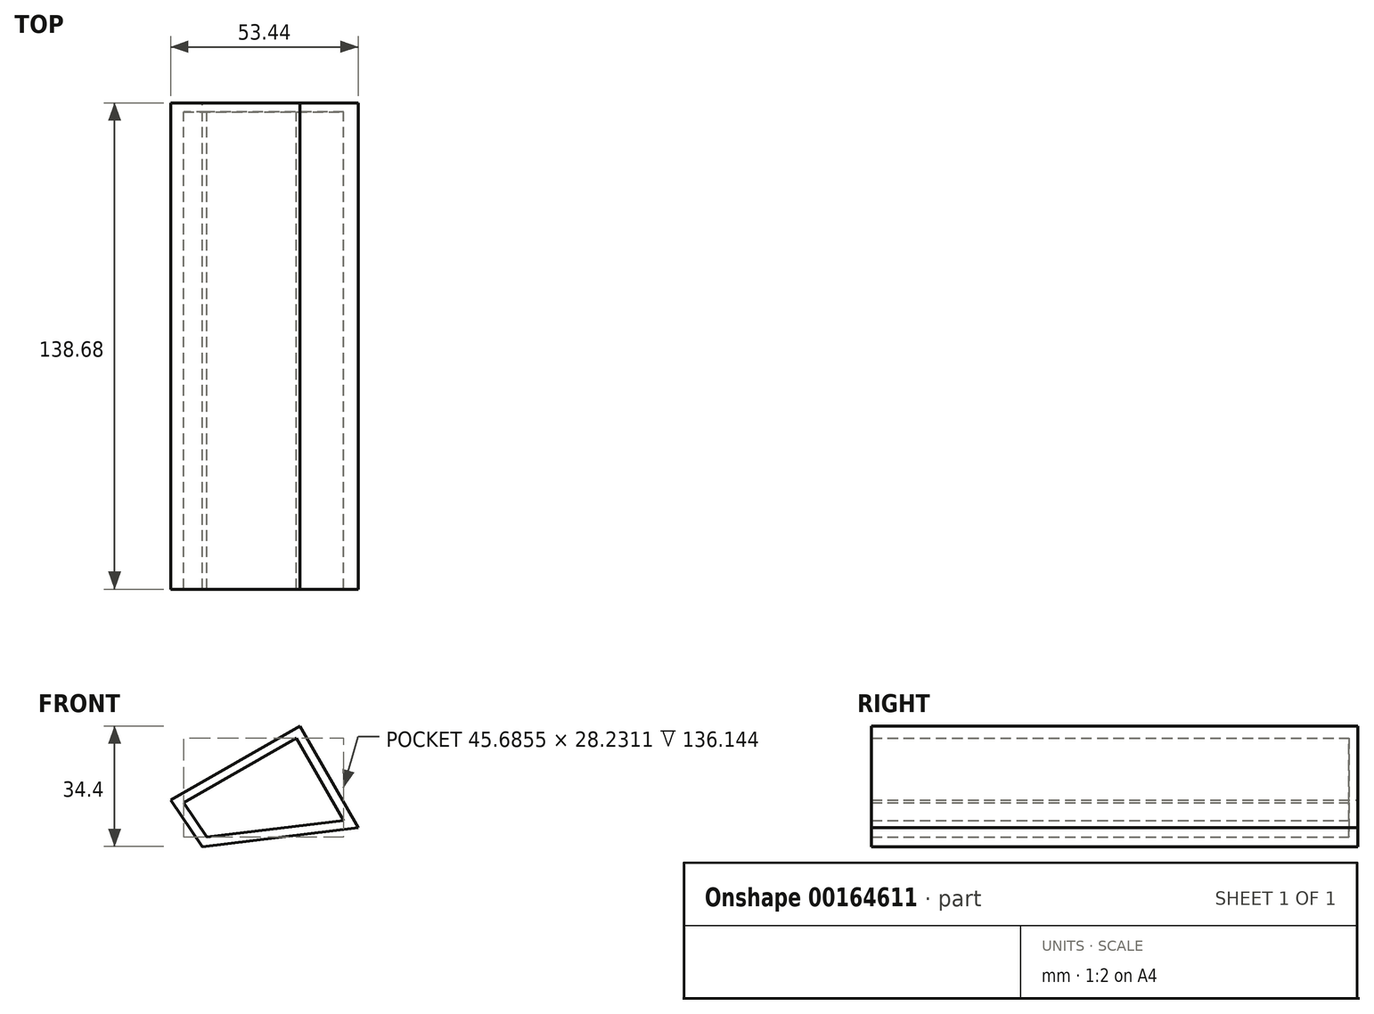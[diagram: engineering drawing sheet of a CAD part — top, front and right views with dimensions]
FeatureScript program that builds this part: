
annotation { "Feature Type Name" : "Feature", "Feature Type Description" : "" }
export const myFeature = defineFeature(function(context is Context, id is Id, definition is map)
    precondition{}
    {
        {
            var Q0;
            Q0=qCreatedBy(makeId("Front.planeOp"),FACE);
            var sketch = newSketch(context, id + "F0", { "sketchPlane" : qUnion([Q0])});
            skLineSegment(sketch, "E0", {"start": v(12.8, 26.67) * mm, "end": v(49.6, 47.74) * mm});
            skLineSegment(sketch, "E1", {"start": v(49.6, 47.74) * mm, "end": v(66.24, 18.69) * mm});
            skLineSegment(sketch, "E2", {"start": v(66.24, 18.69) * mm, "end": v(21.87, 13.34) * mm});
            skLineSegment(sketch, "E3", {"start": v(21.87, 13.34) * mm, "end": v(12.8, 26.67) * mm});
            skSolve(sketch);
        }
        {
            var Q0;
            Q0=makeQuery(id+"F0.imprint","IMPRINT",FACE,{"disambiguationData":[TD([[makeQuery(id+"F0.imprint","IMPRINT",EDGE,{"derivedFrom":sQuery(id+"F0.wireOp",EDGE,"E0")}),-1.0]])]});
            extrude(context, id + "F1", {"entities" : qUnion([Q0]), "depth" : 138.68 * mm});
        }
        {
            var Q0;
            Q0=makeQuery(id+"F1.opExtrude","CAP_FACE",FACE,{"disambiguationData":[OSD([sQuery(id+"F0.wireOp",EDGE,"E0"),sQuery(id+"F0.wireOp",EDGE,"E1"),sQuery(id+"F0.wireOp",EDGE,"E2"),sQuery(id+"F0.wireOp",EDGE,"E3")])],"isStart":false});
            shell(context, id + "F2", {"entities" : qUnion([Q0]), "thickness" : 2.54 * mm});
        }
    });
